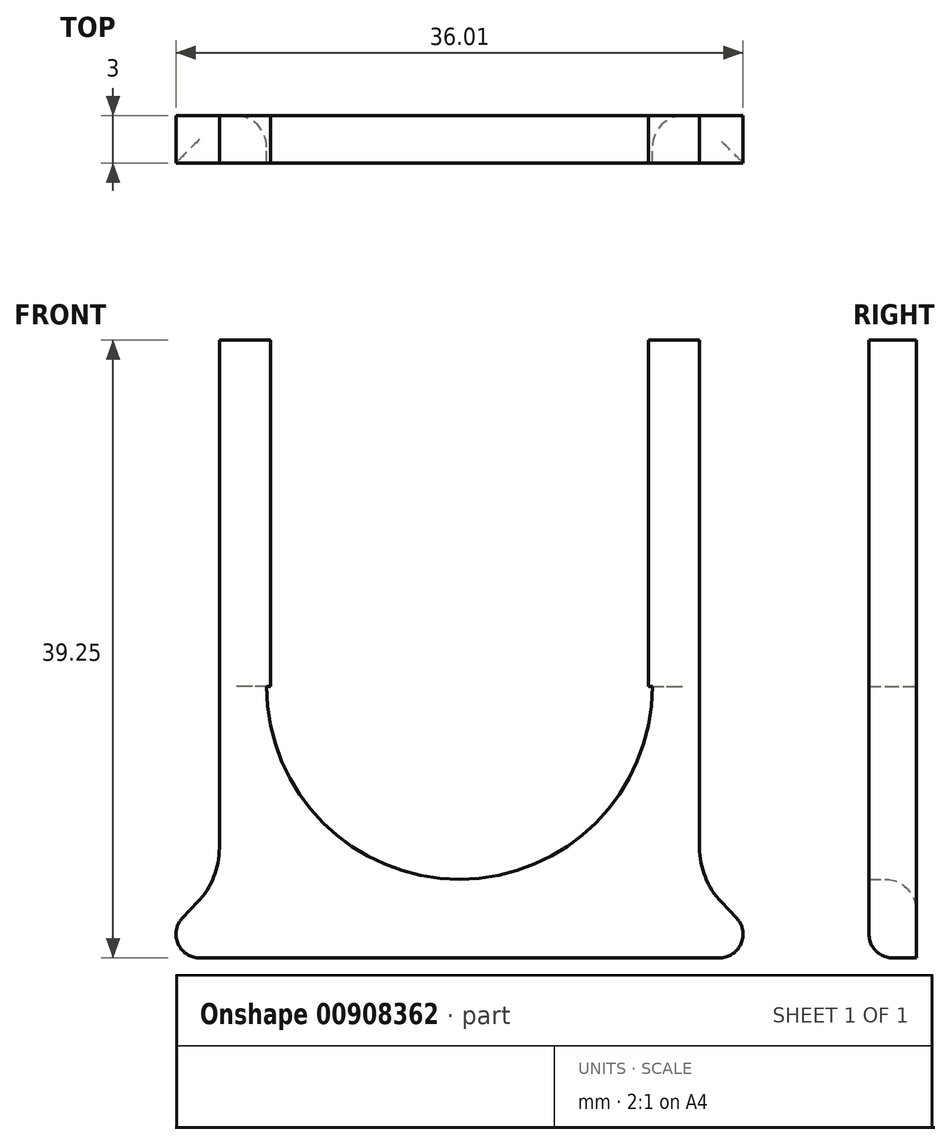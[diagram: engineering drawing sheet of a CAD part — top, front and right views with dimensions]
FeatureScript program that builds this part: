
annotation { "Feature Type Name" : "Feature", "Feature Type Description" : "" }
export const myFeature = defineFeature(function(context is Context, id is Id, definition is map)
    precondition{}
    {
        {
            var Q0;
            Q0=qCreatedBy(makeId("Front.planeOp"),FACE);
            var sketch = newSketch(context, id + "F0", { "sketchPlane" : qUnion([Q0])});
            skArc(sketch, "E0", {"start": v(-20.85, -9.53) * mm, "mid": v(-8.6, -21.78) * mm, "end": v(3.65, -9.53) * mm});
            skLineSegment(sketch, "E1", {"start": v(3.65, -9.53) * mm, "end": v(3.65, 12.47) * mm});
            skArc(sketch, "E2", {"start": v(3.65, 12.47) * mm, "mid": v(-8.6, 24.72) * mm, "end": v(-20.85, 12.47) * mm});
            skLineSegment(sketch, "E3", {"start": v(-20.85, -9.53) * mm, "end": v(-20.85, 12.47) * mm});
            skPoint(sketch, "E4.endSnap0", {"position": v(-8.6, -21.78) * mm});
            skLineSegment(sketch, "E5", {"start": v(-20.85, 12.47) * mm, "end": v(-23.85, 12.47) * mm});
            skLineSegment(sketch, "E6", {"start": v(-23.85, 12.47) * mm, "end": v(-23.85, -9.53) * mm});
            skLineSegment(sketch, "E7", {"start": v(-8.6, -26.78) * mm, "end": v(-28.6, -26.78) * mm});
            skLineSegment(sketch, "E8", {"start": v(-28.6, -26.78) * mm, "end": v(-23.85, -21.78) * mm});
            skLineSegment(sketch, "E9", {"start": v(-23.85, -21.78) * mm, "end": v(-23.85, -9.53) * mm});
            skLineSegment(sketch, "E10", {"start": v(-8.6, -26.78) * mm, "end": v(11.4, -26.78) * mm});
            skLineSegment(sketch, "E11", {"start": v(3.65, 12.47) * mm, "end": v(6.65, 12.47) * mm});
            skLineSegment(sketch, "E12", {"start": v(6.65, 12.47) * mm, "end": v(6.65, -21.78) * mm});
            skLineSegment(sketch, "E13", {"start": v(6.65, -21.78) * mm, "end": v(11.4, -26.78) * mm});
            skSolve(sketch);
        }
        {
            var Q0;
            Q0=makeQuery(id+"F0.imprint","IMPRINT",FACE,{"disambiguationData":[TD([[makeQuery(id+"F0.imprint","IMPRINT",EDGE,{"derivedFrom":sQuery(id+"F0.wireOp",EDGE,"E0")}),-1.0]])]});
            extrude(context, id + "F1", {"entities" : qUnion([Q0]), "depth" : 3 * mm, "offsetDistance" : 25 * mm});
        }
        {
            var Q0;
            Q0=makeQuery(id+"F1.opExtrude","SWEPT_FACE",FACE,{"disambiguationData":[OSD([sQuery(id+"F0.wireOp",EDGE,"E3")])]});
            extrude(context, id + "F2", {"entities" : qUnion([Q0]), "operationType" : NewBodyOperationType.ADD, "depth" : 0.25 * mm, "offsetDistance" : 25 * mm});
        }
        {
            var Q0;
            Q0=makeQuery(id+"F1.opExtrude","SWEPT_FACE",FACE,{"disambiguationData":[OSD([sQuery(id+"F0.wireOp",EDGE,"E1")])]});
            extrude(context, id + "F3", {"entities" : qUnion([Q0]), "operationType" : NewBodyOperationType.ADD, "depth" : 0.25 * mm, "offsetDistance" : 25 * mm});
        }
        {
            var Q0;
            Q0=makeQuery(id+"F1.opExtrude","CAP_EDGE",EDGE,{"disambiguationData":[OSD([sQuery(id+"F0.wireOp",EDGE,"E0")])],"isStart":true});
            fillet(context, id + "F4", {"entities" : qUnion([Q0]), "radius" : 2 * mm, "tangentPropagation" : true, "allowEdgeOverflow" : false});
        }
        {
            var Q0;
            Q0=makeQuery(id+"F1.opExtrude","SWEPT_EDGE",EDGE,{"disambiguationData":[OSD([sQuery(id+"F0.wireOp",EDGE,"E10"),sQuery(id+"F0.wireOp",EDGE,"E13")])]});
            var Q1;
            Q1=makeQuery(id+"F1.opExtrude","SWEPT_EDGE",EDGE,{"disambiguationData":[OSD([sQuery(id+"F0.wireOp",EDGE,"E7"),sQuery(id+"F0.wireOp",EDGE,"E8")])]});
            fillet(context, id + "F5", {"entities" : qUnion([Q0, Q1]), "radius" : 1.5 * mm, "tangentPropagation" : true, "allowEdgeOverflow" : false});
        }
        {
            var Q0;
            Q0=makeQuery(id+"F1.opExtrude","SWEPT_EDGE",EDGE,{"disambiguationData":[OSD([sQuery(id+"F0.wireOp",EDGE,"E8"),sQuery(id+"F0.wireOp",EDGE,"E9")])]});
            var Q1;
            Q1=makeQuery(id+"F1.opExtrude","SWEPT_EDGE",EDGE,{"disambiguationData":[OSD([sQuery(id+"F0.wireOp",EDGE,"E12"),sQuery(id+"F0.wireOp",EDGE,"E13")])]});
            fillet(context, id + "F6", {"entities" : qUnion([Q0, Q1]), "radius" : 5 * mm, "tangentPropagation" : true, "allowEdgeOverflow" : false});
        }
        {
            var Q0;
            Q0=makeQuery(id+"F1.opExtrude","CAP_EDGE",EDGE,{"disambiguationData":[OSD([sQuery(id+"F0.wireOp",EDGE,"E7"),sQuery(id+"F0.wireOp",EDGE,"E10")])],"isStart":false});
            fillet(context, id + "F7", {"entities" : qUnion([Q0]), "radius" : 1.5 * mm, "allowEdgeOverflow" : false});
        }
    });
